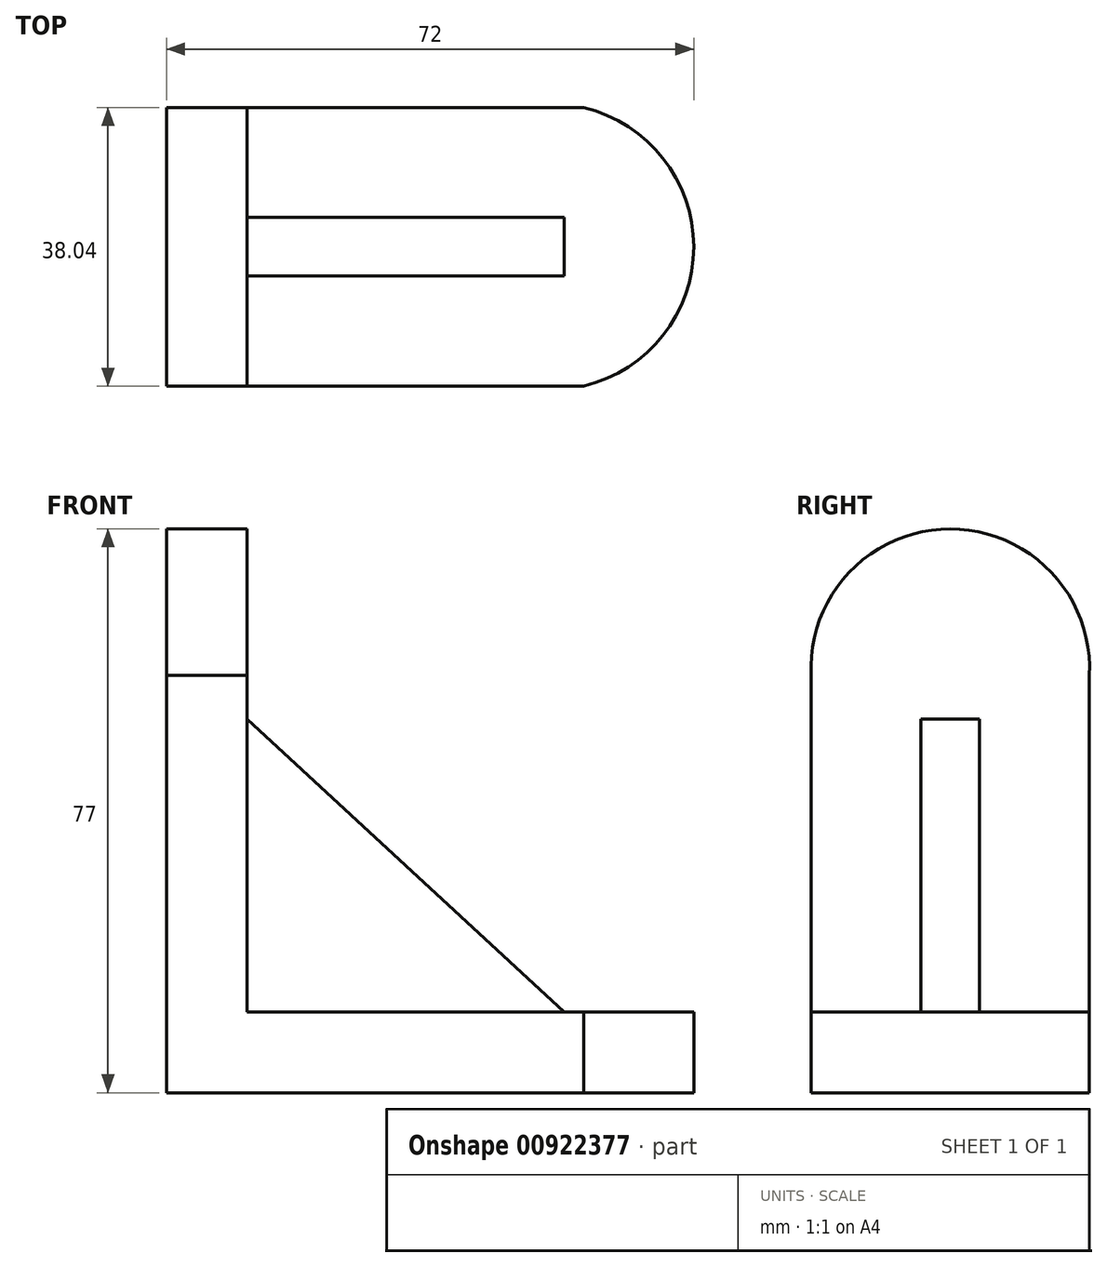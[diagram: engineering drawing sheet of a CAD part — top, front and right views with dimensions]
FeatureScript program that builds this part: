
annotation { "Feature Type Name" : "Feature", "Feature Type Description" : "" }
export const myFeature = defineFeature(function(context is Context, id is Id, definition is map)
    precondition{}
    {
        {
            var Q0;
            Q0=qCreatedBy(makeId("Front.planeOp"),FACE);
            var sketch = newSketch(context, id + "F0", { "sketchPlane" : qUnion([Q0])});
            skLineSegment(sketch, "E0", {"start": v(-31.4, 14.42) * mm, "end": v(-20.4, 14.42) * mm});
            skLineSegment(sketch, "E1", {"start": v(-20.4, 14.42) * mm, "end": v(-20.4, -31.58) * mm});
            skLineSegment(sketch, "E2", {"start": v(-20.4, -31.58) * mm, "end": v(25.6, -31.58) * mm});
            skLineSegment(sketch, "E3", {"start": v(25.6, -31.58) * mm, "end": v(25.6, -42.58) * mm});
            skLineSegment(sketch, "E4", {"start": v(25.6, -42.58) * mm, "end": v(-31.4, -42.58) * mm});
            skLineSegment(sketch, "E5", {"start": v(-31.4, -42.58) * mm, "end": v(-31.4, 14.42) * mm});
            skSolve(sketch);
        }
        {
            var Q0;
            Q0 = qSketchRegion(id + "F0", true);
            extrude(context, id + "F1", {"entities" : qUnion([Q0]), "oppositeDirection" : true, "depth" : 38 * mm, "offsetDistance" : 25 * mm});
        }
        {
            var Q0;
            Q0=makeQuery(id+"F1.opExtrude","SWEPT_FACE",FACE,{"disambiguationData":[OSD([sQuery(id+"F0.wireOp",EDGE,"E1")])]});
            var sketch = newSketch(context, id + "F2", { "sketchPlane" : qUnion([Q0])});
            skLineSegment(sketch, "E6", {"start": v(15, 8.42) * mm, "end": v(15, -31.58) * mm});
            skPoint(sketch, "E6.endSnap0", {"position": v(19, -31.58) * mm});
            skLineSegment(sketch, "E7", {"start": v(15, -31.58) * mm, "end": v(26, -37.23) * mm});
            skLineSegment(sketch, "E8", {"start": v(26, -37.23) * mm, "end": v(34.19, -37.23) * mm});
            skLineSegment(sketch, "E9", {"start": v(34.19, -37.23) * mm, "end": v(23, -31.58) * mm});
            skLineSegment(sketch, "E10", {"start": v(23, -31.58) * mm, "end": v(23, 8.42) * mm});
            skLineSegment(sketch, "E11", {"start": v(23, 8.42) * mm, "end": v(15, 8.42) * mm});
            skSolve(sketch);
        }
        {
            var Q0;
            {var subQ0=sQuery(id+"F2.wireOp",EDGE,"E7");Q0=makeQuery(id+"F2.imprint","IMPRINT",FACE,{"disambiguationData":[TD([[makeQuery(id+"F2.imprint","IMPRINT",EDGE,{"derivedFrom":subQ0}),1.0]])]});}
            var Q1;
            {var subQ0=sQuery(id+"F2.wireOp",EDGE,"E6");Q1=makeQuery(id+"F2.imprint","IMPRINT",FACE,{"disambiguationData":[TD([[makeQuery(id+"F2.imprint","IMPRINT",EDGE,{"derivedFrom":subQ0}),1.0]])]});}
            extrude(context, id + "F3", {"entities" : qUnion([Q0, Q1]), "operationType" : NewBodyOperationType.ADD, "depth" : 43.3 * mm, "offsetDistance" : 25 * mm});
        }
        {
            var Q0;
            Q0=makeQuery(id+"F1.opExtrude","SWEPT_FACE",FACE,{"disambiguationData":[OSD([sQuery(id+"F0.wireOp",EDGE,"E2")])]});
            var sketch = newSketch(context, id + "F4", { "sketchPlane" : qUnion([Q0])});
            skArc(sketch, "E12", {"start": v(25.6, 0) * mm, "mid": v(40.6, 19) * mm, "end": v(25.6, 38) * mm});
            skSolve(sketch);
        }
        {
            var Q0;
            Q0 = qSketchRegion(id + "F4", true);
            var Q1;
            Q1=makeQuery(id+"F4.imprint","IMPRINT",FACE,{"disambiguationData":[TD([[makeQuery(id+"F4.imprint","IMPRINT",EDGE,{"derivedFrom":sQuery(id+"F4.wireOp",EDGE,"E12")}),1.0]])]});
            extrude(context, id + "F5", {"entities" : qUnion([Q0, Q1]), "operationType" : NewBodyOperationType.ADD, "oppositeDirection" : true, "depth" : 11 * mm, "offsetDistance" : 25 * mm});
        }
        {
            var Q0;
            Q0=makeQuery(id+"F1.opExtrude","SWEPT_FACE",FACE,{"disambiguationData":[OSD([sQuery(id+"F0.wireOp",EDGE,"E1")])]});
            var sketch = newSketch(context, id + "F6", { "sketchPlane" : qUnion([Q0])});
            skArc(sketch, "E13", {"start": v(38, 14.42) * mm, "mid": v(19, 34.42) * mm, "end": v(0, 14.42) * mm});
            skSolve(sketch);
        }
        {
            var Q0;
            Q0=makeQuery(id+"F6.imprint","IMPRINT",FACE,{"disambiguationData":[TD([[makeQuery(id+"F6.imprint","IMPRINT",EDGE,{"derivedFrom":sQuery(id+"F6.wireOp",EDGE,"E13")}),1.0]])]});
            extrude(context, id + "F7", {"entities" : qUnion([Q0]), "operationType" : NewBodyOperationType.ADD, "oppositeDirection" : true, "depth" : 11 * mm, "offsetDistance" : 25 * mm});
        }
        {
            var Q0;
            Q0=makeQuery(id+"F3.opExtrude","SWEPT_FACE",FACE,{"disambiguationData":[OSD([sQuery(id+"F2.wireOp",EDGE,"E6")])]});
            var sketch = newSketch(context, id + "F8", { "sketchPlane" : qUnion([Q0])});
            skLineSegment(sketch, "E14", {"start": v(-20.4, 8.42) * mm, "end": v(22.9, 8.42) * mm});
            skLineSegment(sketch, "E15", {"start": v(22.9, 8.42) * mm, "end": v(22.9, -31.58) * mm});
            skLineSegment(sketch, "E16", {"start": v(22.9, -31.58) * mm, "end": v(-20.4, 8.42) * mm});
            skSolve(sketch);
        }
        {
            var Q0;
            Q0=makeQuery(id+"F8.imprint","IMPRINT",FACE,{"disambiguationData":[TD([[makeQuery(id+"F8.imprint","IMPRINT",EDGE,{"derivedFrom":sQuery(id+"F8.wireOp",EDGE,"E14")}),1.0]])]});
            extrude(context, id + "F9", {"entities" : qUnion([Q0]), "operationType" : NewBodyOperationType.REMOVE, "oppositeDirection" : true, "depth" : 42.4 * mm, "offsetDistance" : 25 * mm});
        }
    });
